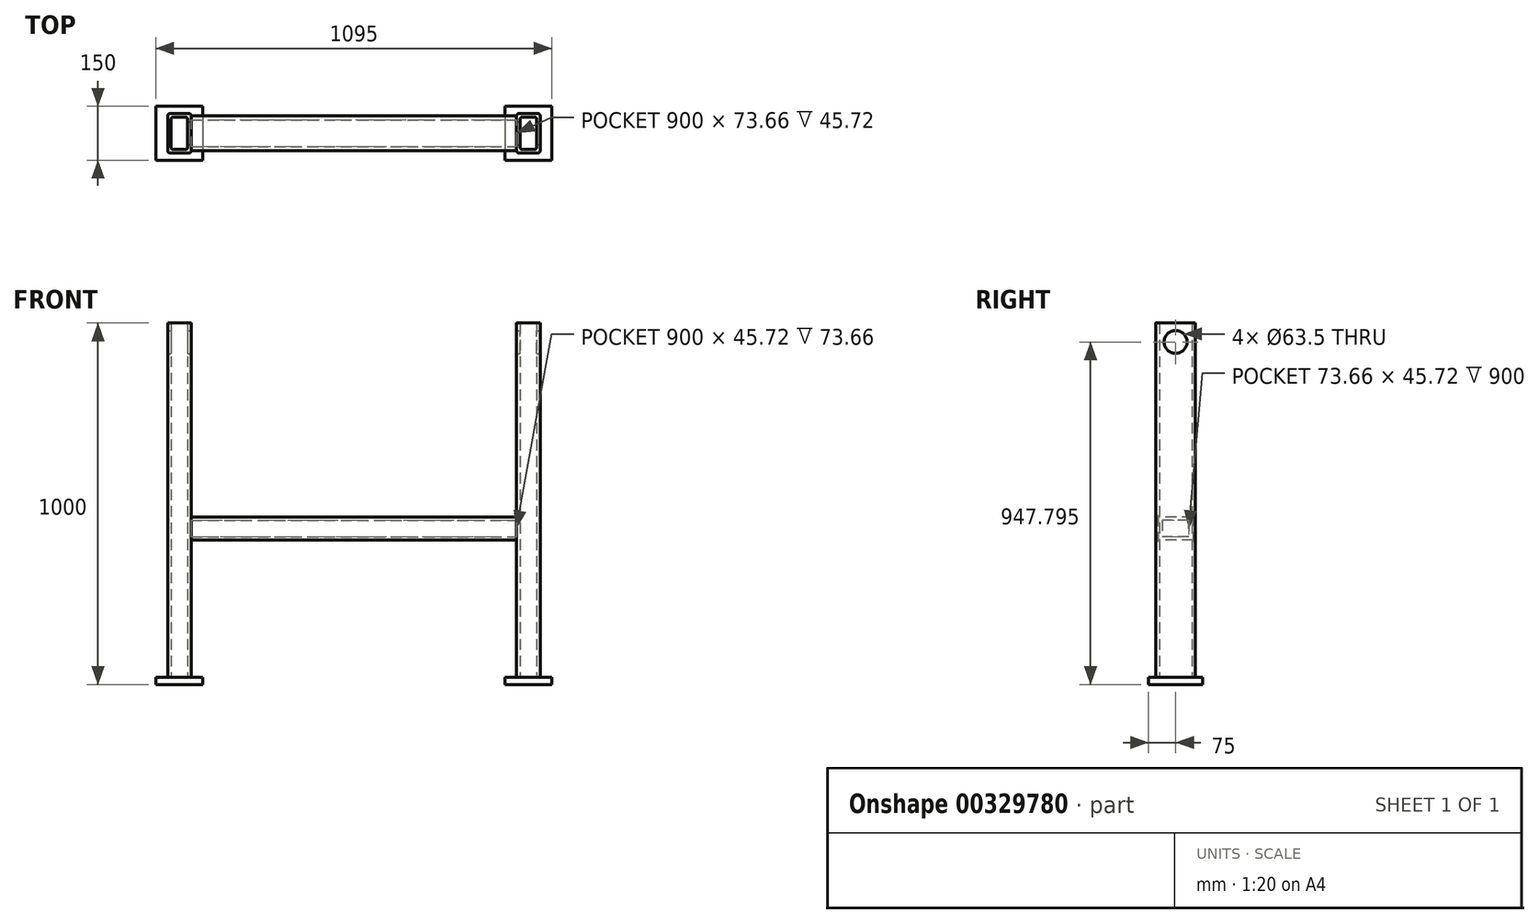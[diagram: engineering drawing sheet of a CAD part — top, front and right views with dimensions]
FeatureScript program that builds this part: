
annotation { "Feature Type Name" : "Feature", "Feature Type Description" : "" }
export const myFeature = defineFeature(function(context is Context, id is Id, definition is map)
    precondition{}
    {
        {
            var Q0;
            Q0=qCreatedBy(makeId("Top.planeOp"),FACE);
            var sketch = newSketch(context, id + "F0", { "sketchPlane" : qUnion([Q0])});
            skLineSegment(sketch, "E0.bottom", {"start": v(450, 75) * mm, "end": v(580, 75) * mm});
            skLineSegment(sketch, "E0.top", {"start": v(450, -75) * mm, "end": v(580, -75) * mm});
            skLineSegment(sketch, "E0.left", {"start": v(450, 75) * mm, "end": v(450, -75) * mm});
            skLineSegment(sketch, "E0.right", {"start": v(580, 75) * mm, "end": v(580, -75) * mm});
            skSolve(sketch);
        }
        {
            var Q0;
            Q0=makeQuery(id+"F0.imprint","IMPRINT",FACE,{"disambiguationData":[TD([[makeQuery(id+"F0.imprint","IMPRINT",EDGE,{"derivedFrom":sQuery(id+"F0.wireOp",EDGE,"E0.bottom")}),-1.0]])]});
            extrude(context, id + "F1", {"entities" : qUnion([Q0]), "depth" : 20 * mm});
        }
        {
            var Q0;
            Q0=makeQuery(id+"F1.opExtrude","CAP_FACE",FACE,{"disambiguationData":[OSD([sQuery(id+"F0.wireOp",EDGE,"E0.bottom"),sQuery(id+"F0.wireOp",EDGE,"E0.top"),sQuery(id+"F0.wireOp",EDGE,"E0.left"),sQuery(id+"F0.wireOp",EDGE,"E0.right")])],"isStart":false});
            var sketch = newSketch(context, id + "F2", { "sketchPlane" : qUnion([Q0])});
            skLineSegment(sketch, "E1.bottom", {"start": v(482.5, 55) * mm, "end": v(547.5, 55) * mm});
            skLineSegment(sketch, "E1.top", {"start": v(482.5, -55) * mm, "end": v(547.5, -55) * mm});
            skLineSegment(sketch, "E1.left", {"start": v(482.5, 55) * mm, "end": v(482.5, -55) * mm});
            skLineSegment(sketch, "E1.right", {"start": v(547.5, 55) * mm, "end": v(547.5, -55) * mm});
            skLineSegment(sketch, "E2.bottom", {"start": v(492.5, 45) * mm, "end": v(537.5, 45) * mm});
            skLineSegment(sketch, "E2.top", {"start": v(492.5, -45) * mm, "end": v(537.5, -45) * mm});
            skLineSegment(sketch, "E2.left", {"start": v(492.5, 45) * mm, "end": v(492.5, -45) * mm});
            skLineSegment(sketch, "E2.right", {"start": v(537.5, 45) * mm, "end": v(537.5, -45) * mm});
            skSolve(sketch);
        }
        {
            var Q0;
            Q0=makeQuery(id+"F2.imprint","IMPRINT",FACE,{"disambiguationData":[TD([[makeQuery(id+"F2.imprint","IMPRINT",EDGE,{"derivedFrom":sQuery(id+"F2.wireOp",EDGE,"E1.bottom")}),-1.0]])]});
            extrude(context, id + "F3", {"entities" : qUnion([Q0]), "operationType" : NewBodyOperationType.ADD, "depth" : 980 * mm});
        }
        {
            var Q0;
            Q0=makeQuery(id+"F3.opExtrude","SWEPT_EDGE",EDGE,{"disambiguationData":[OSD([sQuery(id+"F2.wireOp",EDGE,"E1.top"),sQuery(id+"F2.wireOp",EDGE,"E1.right")])]});
            var Q1;
            Q1=makeQuery(id+"F3.opExtrude","SWEPT_EDGE",EDGE,{"disambiguationData":[OSD([sQuery(id+"F2.wireOp",EDGE,"E1.top"),sQuery(id+"F2.wireOp",EDGE,"E1.left")])]});
            var Q2;
            Q2=makeQuery(id+"F3.opExtrude","SWEPT_EDGE",EDGE,{"disambiguationData":[OSD([sQuery(id+"F2.wireOp",EDGE,"E1.bottom"),sQuery(id+"F2.wireOp",EDGE,"E1.right")])]});
            var Q3;
            Q3=makeQuery(id+"F3.opExtrude","SWEPT_EDGE",EDGE,{"disambiguationData":[OSD([sQuery(id+"F2.wireOp",EDGE,"E1.bottom"),sQuery(id+"F2.wireOp",EDGE,"E1.left")])]});
            fillet(context, id + "F4", {"entities" : qUnion([Q0, Q1, Q2, Q3]), "radius" : 7 * mm, "tangentPropagation" : true, "allowEdgeOverflow" : false});
        }
        {
            var Q0;
            Q0=makeQuery(id+"F3.opExtrude","SWEPT_EDGE",EDGE,{"disambiguationData":[OSD([sQuery(id+"F2.wireOp",EDGE,"E2.bottom"),sQuery(id+"F2.wireOp",EDGE,"E2.left")])]});
            var Q1;
            Q1=makeQuery(id+"F3.opExtrude","SWEPT_EDGE",EDGE,{"disambiguationData":[OSD([sQuery(id+"F2.wireOp",EDGE,"E2.top"),sQuery(id+"F2.wireOp",EDGE,"E2.left")])]});
            var Q2;
            Q2=makeQuery(id+"F3.opExtrude","SWEPT_EDGE",EDGE,{"disambiguationData":[OSD([sQuery(id+"F2.wireOp",EDGE,"E2.top"),sQuery(id+"F2.wireOp",EDGE,"E2.right")])]});
            var Q3;
            Q3=makeQuery(id+"F3.opExtrude","SWEPT_EDGE",EDGE,{"disambiguationData":[OSD([sQuery(id+"F2.wireOp",EDGE,"E2.bottom"),sQuery(id+"F2.wireOp",EDGE,"E2.right")])]});
            fillet(context, id + "F5", {"entities" : qUnion([Q0, Q1, Q2, Q3]), "radius" : 5.08 * mm, "tangentPropagation" : true, "allowEdgeOverflow" : false});
        }
        {
            var Q0;
            Q0=makeQuery(id+"F3.opExtrude","SWEPT_FACE",FACE,{"disambiguationData":[OSD([sQuery(id+"F2.wireOp",EDGE,"E1.left")])]});
            var sketch = newSketch(context, id + "F6", { "sketchPlane" : qUnion([Q0])});
            skLineSegment(sketch, "E3.bottom", {"start": v(-48, 400) * mm, "end": v(48, 400) * mm});
            skLineSegment(sketch, "E3.top", {"start": v(-48, 463.5) * mm, "end": v(48, 463.5) * mm});
            skLineSegment(sketch, "E3.left", {"start": v(-48, 463.5) * mm, "end": v(-48, 400) * mm});
            skLineSegment(sketch, "E3.right", {"start": v(48, 463.5) * mm, "end": v(48, 400) * mm});
            skLineSegment(sketch, "E4.bottom", {"start": v(-36.57, 454.6) * mm, "end": v(37.09, 454.6) * mm});
            skLineSegment(sketch, "E4.top", {"start": v(-36.57, 408.9) * mm, "end": v(37.1, 408.9) * mm});
            skLineSegment(sketch, "E4.left", {"start": v(-36.57, 454.6) * mm, "end": v(-36.57, 408.9) * mm});
            skLineSegment(sketch, "E4.right", {"start": v(37.09, 454.61) * mm, "end": v(37.1, 408.9) * mm});
            skSolve(sketch);
        }
        {
            var Q0;
            Q0 = qSketchRegion(id + "F6", true);
            extrude(context, id + "F7", {"entities" : qUnion([Q0]), "operationType" : NewBodyOperationType.ADD, "depth" : 450 * mm});
        }
        {
            var Q0;
            Q0=makeQuery(id+"F7.opExtrude","CAP_EDGE",EDGE,{"disambiguationData":[OSD([sQuery(id+"F6.wireOp",EDGE,"E3.top")])],"isStart":true});
            fillet(context, id + "F8", {"entities" : qUnion([Q0]), "radius" : 5 * mm, "tangentPropagation" : true, "allowEdgeOverflow" : false});
        }
        {
            var Q0;
            Q0=makeQuery(id+"F7.opExtrude","CAP_EDGE",EDGE,{"disambiguationData":[OSD([sQuery(id+"F6.wireOp",EDGE,"E3.bottom")])],"isStart":true});
            fillet(context, id + "F9", {"entities" : qUnion([Q0]), "radius" : 5 * mm, "tangentPropagation" : true, "allowEdgeOverflow" : false});
        }
        {
            var Q0;
            Q0=makeQuery(id+"F7.opExtrude","CAP_FACE",FACE,{"disambiguationData":[OSD([sQuery(id+"F6.wireOp",EDGE,"E3.bottom"),sQuery(id+"F6.wireOp",EDGE,"E3.top"),sQuery(id+"F6.wireOp",EDGE,"E3.left"),sQuery(id+"F6.wireOp",EDGE,"E3.right")])],"isStart":false});
            var sketch = newSketch(context, id + "F10", { "sketchPlane" : qUnion([Q0])});
            skLineSegment(sketch, "E5", {"start": v(48, 463.5) * mm, "end": v(48, 1000) * mm});
            skLineSegment(sketch, "E6", {"start": v(48, 1000) * mm, "end": v(-52, 1000) * mm});
            skLineSegment(sketch, "E7", {"start": v(-52, 1000) * mm, "end": v(-48, 463.5) * mm});
            skLineSegment(sketch, "E8", {"start": v(-48, 463.5) * mm, "end": v(-48, 20) * mm});
            skLineSegment(sketch, "E9", {"start": v(-48, 20) * mm, "end": v(48, 20) * mm});
            skLineSegment(sketch, "E10", {"start": v(48, 20) * mm, "end": v(48, 463.5) * mm});
            skSolve(sketch);
        }
        {
            var Q0;
            Q0=makeQuery(id+"F1.opExtrude","SWEPT_BODY",BODY,{"disambiguationData":[OSD([sQuery(id+"F0.wireOp",EDGE,"E0.bottom"),sQuery(id+"F0.wireOp",EDGE,"E0.top"),sQuery(id+"F0.wireOp",EDGE,"E0.left"),sQuery(id+"F0.wireOp",EDGE,"E0.right")])]});
            var Q1;
            Q1=makeQuery(id+"F10.imprint","IMPRINT",FACE,{"disambiguationData":[TD([[makeQuery(id+"F10.imprint","IMPRINT",EDGE,{"derivedFrom":sQuery(id+"F10.wireOp",EDGE,"E5")}),1.0]])]});
            mirror(context, id + "F11", {"operationType" : NewBodyOperationType.ADD, "entities" : qUnion([Q0]), "mirrorPlane" : qUnion([Q1])});
        }
        {
            var Q0;
            Q0=makeQuery(id+"F3.opExtrude","SWEPT_FACE",FACE,{"disambiguationData":[OSD([sQuery(id+"F2.wireOp",EDGE,"E1.right")])]});
            var sketch = newSketch(context, id + "F12", { "sketchPlane" : qUnion([Q0])});
            skCircle(sketch, "E11", {"center": v(0, 947.8) * mm, "radius": 35.53 * mm});
            skPoint(sketch, "E11.centerSnap0", {"position": v(0, 1000) * mm});
            skSolve(sketch);
        }
        {
            var Q0;
            Q0=sQuery(id+"F12.wireOp",VERTEX,"E11.center");
            var Q1;
            Q1=makeQuery(id+"F1.opExtrude","SWEPT_BODY",BODY,{"disambiguationData":[OSD([sQuery(id+"F0.wireOp",EDGE,"E0.bottom"),sQuery(id+"F0.wireOp",EDGE,"E0.top"),sQuery(id+"F0.wireOp",EDGE,"E0.left"),sQuery(id+"F0.wireOp",EDGE,"E0.right")])]});
            hole(context, id + "F13", {"style" : HoleStyle.SIMPLE, "endStyle" : HoleEndStyle.THROUGH, "holeDiameter" : 63.5 * mm, "tappedDepth" : 12.7 * mm, "tapClearance" : 3, "locations" : qUnion([Q0]), "scope" : qUnion([Q1])});
        }
    });
